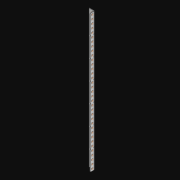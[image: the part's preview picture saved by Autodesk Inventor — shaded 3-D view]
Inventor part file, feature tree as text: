
AUTODESK INVENTOR PART (.ipt)
format: ipt  version: 2021 (Build 250183000, 183)  size: 1,315,328 bytes
history: native  units: in
note: dims shown in document units (in); Inventor stores cm internally (conversion verified against a paired STEP export)
features: extrude x71, other x70, sketch x3, pattern_linear x2, sheet_metal_op x1
ambient origin geometry x8: Origin, YZ Plane, XZ Plane, XY Plane, X Axis, Y Axis, Z Axis, Center Point
bodies: Solid1 (feature_tree)
feature tree (147):
  pattern_linear  "Rectangular Pattern1"  Spacing1=0.063in  [1 undecoded]
  pattern_linear  "Rectangular Pattern3"  Spacing1=0.5in  [1 undecoded]
  extrude  "Extrusion1"  Depth=0.5in
  sketch  "Sketch1"  dims[d0=0.182in]
  other  "Srf1"
  sketch  "Sketch3"  dims[d1=0.063in d2=0.0in]
  other  "Srf3"
  other  "Srf4"
  other  "Srf5"
  other  "Srf6"
  other  "Srf7"
  other  "Srf8"
  other  "Srf9"
  other  "Srf10"
  other  "Srf11"
  other  "Srf12"
  other  "Srf13"
  other  "Srf14"
  other  "Srf15"
  other  "Srf16"
  other  "Srf17"
  other  "Srf18"
  other  "Srf19"
  other  "Srf20"
  other  "Srf21"
  other  "Srf22"
  other  "Srf23"
  other  "Srf24"
  other  "Srf25"
  other  "Srf26"
  other  "Srf27"
  other  "Srf28"
  other  "Srf29"
  other  "Srf30"
  other  "Srf31"
  other  "Srf32"
  other  "Srf33"
  other  "Srf34"
  other  "Srf35"
  other  "Srf36"
  other  "Srf37"
  other  "Srf142"
  other  "Srf143"
  other  "Srf144"
  other  "Srf145"
  other  "Srf146"
  other  "Srf147"
  other  "Srf148"
  other  "Srf149"
  other  "Srf150"
  other  "Srf151"
  other  "Srf152"
  other  "Srf153"
  other  "Srf154"
  other  "Srf155"
  other  "Srf156"
  other  "Srf157"
  other  "Srf158"
  other  "Srf159"
  other  "Srf160"
  other  "Srf161"
  other  "Srf162"
  other  "Srf163"
  other  "Srf164"
  other  "Srf165"
  other  "Srf166"
  other  "Srf167"
  other  "Srf168"
  other  "Srf169"
  other  "Srf170"
  other  "Srf171"
  other  "Srf172"
  other  "Srf173"
  other  "Srf174"
  other  "Srf175"
  sketch  "Sketch4"  dims[d6=0.182in d7=0.063in d8=0.0in d11=0.5in d12=0.3937in d14=0.5in d18=13.7795in d20=0.5in d21=0.841in d22=0.0in]
  sheet_metal_op  "Fold1"
  extrude  "ExtrusionSrf1"  Depth=0.5in
  extrude  "ExtrusionSrf3"  Depth=0.5in TaperAngle=0.0deg
  extrude  "ExtrusionSrf4"  [1 undecoded]
  extrude  "ExtrusionSrf5"  [1 undecoded]
  extrude  "ExtrusionSrf6"  [1 undecoded]
  extrude  "ExtrusionSrf7"  [1 undecoded]
  extrude  "ExtrusionSrf8"  [1 undecoded]
  extrude  "ExtrusionSrf9"  [1 undecoded]
  extrude  "ExtrusionSrf10"  [1 undecoded]
  extrude  "ExtrusionSrf11"  [1 undecoded]
  extrude  "ExtrusionSrf12"  [1 undecoded]
  extrude  "ExtrusionSrf13"  [1 undecoded]
  extrude  "ExtrusionSrf14"  [1 undecoded]
  extrude  "ExtrusionSrf15"  [1 undecoded]
  extrude  "ExtrusionSrf16"  [1 undecoded]
  extrude  "ExtrusionSrf17"  [1 undecoded]
  extrude  "ExtrusionSrf18"  [1 undecoded]
  extrude  "ExtrusionSrf19"  [1 undecoded]
  extrude  "ExtrusionSrf20"  [1 undecoded]
  extrude  "ExtrusionSrf21"  [1 undecoded]
  extrude  "ExtrusionSrf22"  [1 undecoded]
  extrude  "ExtrusionSrf23"  [1 undecoded]
  extrude  "ExtrusionSrf24"  [1 undecoded]
  extrude  "ExtrusionSrf25"  [1 undecoded]
  extrude  "ExtrusionSrf26"  [1 undecoded]
  extrude  "ExtrusionSrf27"  [1 undecoded]
  extrude  "ExtrusionSrf28"  [1 undecoded]
  extrude  "ExtrusionSrf29"  [1 undecoded]
  extrude  "ExtrusionSrf30"  [1 undecoded]
  extrude  "ExtrusionSrf31"  [1 undecoded]
  extrude  "ExtrusionSrf32"  [1 undecoded]
  extrude  "ExtrusionSrf33"  [1 undecoded]
  extrude  "ExtrusionSrf34"  [1 undecoded]
  extrude  "ExtrusionSrf35"  [1 undecoded]
  extrude  "ExtrusionSrf36"  [1 undecoded]
  extrude  "ExtrusionSrf37"  [1 undecoded]
  extrude  "ExtrusionSrf142"  [1 undecoded]
  extrude  "ExtrusionSrf143"  [1 undecoded]
  extrude  "ExtrusionSrf144"  [1 undecoded]
  extrude  "ExtrusionSrf145"  [1 undecoded]
  extrude  "ExtrusionSrf146"  [1 undecoded]
  extrude  "ExtrusionSrf147"  [1 undecoded]
  extrude  "ExtrusionSrf148"  [1 undecoded]
  extrude  "ExtrusionSrf149"  [1 undecoded]
  extrude  "ExtrusionSrf150"  [1 undecoded]
  extrude  "ExtrusionSrf151"  [1 undecoded]
  extrude  "ExtrusionSrf152"  [1 undecoded]
  extrude  "ExtrusionSrf153"  [1 undecoded]
  extrude  "ExtrusionSrf154"  [1 undecoded]
  extrude  "ExtrusionSrf155"  [1 undecoded]
  extrude  "ExtrusionSrf156"  [1 undecoded]
  extrude  "ExtrusionSrf157"  [1 undecoded]
  extrude  "ExtrusionSrf158"  [1 undecoded]
  extrude  "ExtrusionSrf159"  [1 undecoded]
  extrude  "ExtrusionSrf160"  [1 undecoded]
  extrude  "ExtrusionSrf161"  [1 undecoded]
  extrude  "ExtrusionSrf162"  [1 undecoded]
  extrude  "ExtrusionSrf163"  [1 undecoded]
  extrude  "ExtrusionSrf164"  [1 undecoded]
  extrude  "ExtrusionSrf165"  [1 undecoded]
  extrude  "ExtrusionSrf166"  [1 undecoded]
  extrude  "ExtrusionSrf167"  [1 undecoded]
  extrude  "ExtrusionSrf168"  [1 undecoded]
  extrude  "ExtrusionSrf169"  [1 undecoded]
  extrude  "ExtrusionSrf170"  [1 undecoded]
  extrude  "ExtrusionSrf171"  [1 undecoded]
  extrude  "ExtrusionSrf172"  [1 undecoded]
  extrude  "ExtrusionSrf173"  [1 undecoded]
  extrude  "ExtrusionSrf174"  [1 undecoded]
  extrude  "ExtrusionSrf175"  [1 undecoded]
note: 70 required parameter values undecoded (feature->parameter linkage not recoverable at this tier; creation-order binding heuristic only, values carry confidence <= 0.55)
